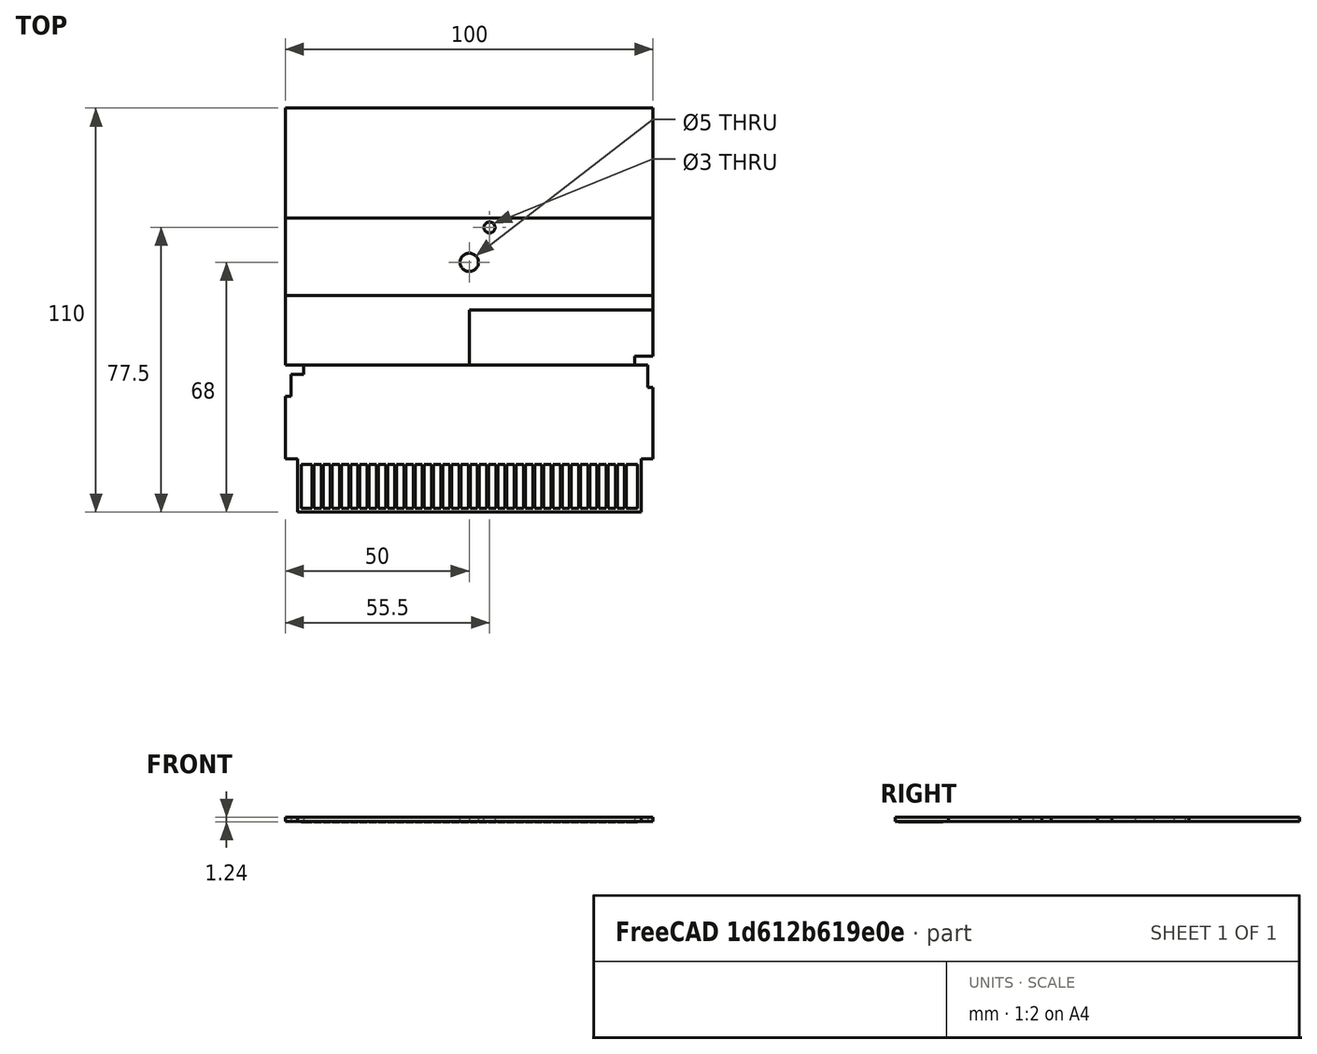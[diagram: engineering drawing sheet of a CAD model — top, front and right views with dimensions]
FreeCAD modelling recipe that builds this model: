
FCSTD DOCUMENT  (FreeCAD 0.20R29177 +426 (Git))
Label: NES-EWROM-01
License: Other
objects: TechDraw::DrawViewDimension×33, Sketcher::SketchObject×7, Part::Face×7, Part::Extrusion×5, App::Part×3, TechDraw::DrawProjGroupItem×3, Part::FeaturePython×2, TechDraw::DrawSVGTemplate×2, TechDraw::DrawPage×2, PartDesign::CoordinateSystem×1, TechDraw::DrawProjGroup×1, Spreadsheet::Sheet×1, TechDraw::DrawViewSpreadsheet×1
note: 22 computed .brp shape members not serialized (recipe doc carries the construction recipe); baked Part::Feature solids carry a one-line shape summary decoded from their .brp

FEATURE [PartDesign::CoordinateSystem] Local_CS_dc13
  AttacherType = Attacher::AttachEngine3D
  MapMode = 2
  Support = -> [X_Axis001]
FEATURE [App::Part] Step_Models_dc13
  Origin = -> Origin002
FEATURE [Part::FeaturePython] TopPads  # a2plus imported part (geometry in sourceFile) (typed FeaturePython)
  Placement = pos=(0,0,0.02) rot=(0,0,1;0rad)
  fixedPosition = true
FEATURE [Part::FeaturePython] BotPads  # a2plus imported part (geometry in sourceFile) (typed FeaturePython)
  Placement = pos=(0,0,0.38) rot=(0,0,1;0rad)
  fixedPosition = true
FEATURE [Sketcher::SketchObject] Sketch  label="TopSolderMask"
  FullyConstrained = true
  sketch-geometry (4):
    g0: LineSegment StartX=-46.75 StartY=-8 StartZ=0 EndX=46.75 EndY=-8 EndZ=0
    g1: LineSegment StartX=46.75 StartY=-8 StartZ=0 EndX=46.75 EndY=-14.5 EndZ=0
    g2: LineSegment StartX=46.75 StartY=-14.5 StartZ=0 EndX=-46.75 EndY=-14.5 EndZ=0
    g3: LineSegment StartX=-46.75 StartY=-14.5 StartZ=0 EndX=-46.75 EndY=-8 EndZ=0
  constraints (11):
    c: Coincident(g0,g1)
    c: Coincident(g1,g2)
    c: Coincident(g2,g3)
    c: Coincident(g3,g0)
    c: Horizontal(g2)
    c: Vertical(g1)
    c: Vertical(g3)
    c: DistanceY(g0,g-1) = 8
    c: DistanceY(g3,g3) = 6.5
    c: DistanceX(g2,g2) = 93.5
    c: Symmetric(g0,g0,g-2)
FEATURE [Part::Face] Face  label="TopSoldermask"
  FaceMakerClass = Part::FaceMakerBullseye
  Placement = pos=(0,0,0.02) rot=(0,0,1;0rad)
  Sources = -> [Sketch]
FEATURE [Sketcher::SketchObject] Sketch001  label="BotSoldermask"
  FullyConstrained = true
  Placement = pos=(0,0,-1.2) rot=(0,0,1;0rad)
  sketch-geometry (4):
    g0: LineSegment StartX=-46.75 StartY=-3.5 StartZ=0 EndX=46.75 EndY=-3.5 EndZ=0
    g1: LineSegment StartX=46.75 StartY=-3.5 StartZ=0 EndX=46.75 EndY=-14.5 EndZ=0
    g2: LineSegment StartX=46.75 StartY=-14.5 StartZ=0 EndX=-46.75 EndY=-14.5 EndZ=0
    g3: LineSegment StartX=-46.75 StartY=-14.5 StartZ=0 EndX=-46.75 EndY=-3.5 EndZ=0
  constraints (11):
    c: Coincident(g0,g1)
    c: Coincident(g1,g2)
    c: Coincident(g2,g3)
    c: Coincident(g3,g0)
    c: Horizontal(g0)
    c: Vertical(g1)
    c: Vertical(g3)
    c: Symmetric(g1,g2,g-2)
    c: DistanceY(g3,g3) = 11
    c: DistanceY(g0,g-1) = 3.5
    c: DistanceX(g2,g2) = 93.5
FEATURE [Part::Face] Face001  label="BotSolderMask"
  FaceMakerClass = Part::FaceMakerBullseye
  Placement = pos=(0,0,-0.02) rot=(0,0,1;0rad)
  Sources = -> [Sketch001]
FEATURE [TechDraw::DrawSVGTemplate] Template002  label="Template"
  EditableTexts = AUTHOR_NAME=Persune; DRAWING_TITLE=NES-EWROM-01; FC-DATE=2023-02-12; FC-REV=0.0.6; FC-SC=1:1; FC-SH=1/2; FC-SI=A4; FreeCAD_DRAWING=Unit in millimeters. Tolerance ±0.05mm.; SI-1=Outline made in Kicad. Drafting made in FreeCad.; SI-3=Base measurements assume 0.05 mm grid.
  Height = 210
  Orientation = 1
  Width = 297
FEATURE [Sketcher::SketchObject] Sketch002  label="CutTier1"
  FullyConstrained = true
  sketch-geometry (15):
    g0: LineSegment StartX=-50 StartY=0 StartZ=0 EndX=-46.75 EndY=0 EndZ=0
    g1: LineSegment StartX=-46.75 StartY=0 StartZ=0 EndX=-46.75 EndY=-14.5 EndZ=0
    g2: LineSegment StartX=46.75 StartY=-14.5 StartZ=0 EndX=46.75 EndY=0 EndZ=0
    g3: LineSegment StartX=46.75 StartY=0 StartZ=0 EndX=50 EndY=0 EndZ=0
    g4: LineSegment StartX=-50 StartY=17 StartZ=0 EndX=-50 EndY=0 EndZ=0
    g5: LineSegment StartX=-46.75 StartY=-14.5 StartZ=0 EndX=46.75 EndY=-14.5 EndZ=0
    g6: LineSegment StartX=-50 StartY=17 StartZ=0 EndX=-48.5 EndY=17 EndZ=0
    g7: LineSegment StartX=-48.5 StartY=17 StartZ=0 EndX=-48.5 EndY=23 EndZ=0
    g8: LineSegment StartX=-48.5 StartY=23 StartZ=0 EndX=-45 EndY=23 EndZ=0
    g9: LineSegment StartX=-45 StartY=23 StartZ=0 EndX=-45 EndY=25.5 EndZ=0
    g10: LineSegment StartX=50 StartY=0 StartZ=0 EndX=50 EndY=19.5 EndZ=0
    g11: LineSegment StartX=50 StartY=19.5 StartZ=0 EndX=48.5 EndY=19.5 EndZ=0
    g12: LineSegment StartX=45 StartY=25.5 StartZ=0 EndX=-45 EndY=25.5 EndZ=0
    g13: LineSegment StartX=45 StartY=25.5 StartZ=0 EndX=48.5 EndY=25.5 EndZ=0
    g14: LineSegment StartX=48.5 StartY=25.5 StartZ=0 EndX=48.5 EndY=19.5 EndZ=0
  constraints (45):
    c: PointOnObject(g0,g-1)
    c: PointOnObject(g0,g-1)
    c: Coincident(g1,g0)
    c: Vertical(g1)
    c: Vertical(g2)
    c: PointOnObject(g3,g-1)
    c: Horizontal(g3)
    c: Coincident(g4,g0)
    c: Vertical(g4)
    c: Symmetric(g0,g2,g-2)
    c: DistanceY(g1,g1) = 14.5
    c: Coincident(g5,g1)
    c: Coincident(g5,g2)
    c: Horizontal(g5)
    c: DistanceX(g5,g5) = 93.5
    c: DistanceX(g0,g0) = 3.25
    c: DistanceX(g0,g3) = 100
    c: DistanceY(g4,g4) = 17
    c: Coincident(g6,g4)
    c: Horizontal(g6)
    c: DistanceX(g6,g6) = 1.5
    c: Coincident(g7,g6)
    c: Vertical(g7)
    c: DistanceY(g7,g7) = 6
    c: Coincident(g8,g7)
    c: Horizontal(g8)
    c: DistanceX(g8,g8) = 3.5
    c: DistanceX(g3,g3) = 3.25
    c: Coincident(g8,g9)
    c: Vertical(g9)
    c: DistanceY(g9,g9) = 2.5
    c: Coincident(g10,g3)
    c: Vertical(g10)
    c: DistanceY(g10,g10) = 19.5
    c: Coincident(g10,g11)
    c: Horizontal(g11)
    c: Coincident(g12,g9)
    c: Horizontal(g12)
    c: DistanceX(g12,g12) = 90
    c: DistanceX(g11,g11) = 1.5
    c: Coincident(g12,g13)
    c: Horizontal(g13)
    c: Coincident(g13,g14)
    c: Coincident(g14,g11)
    c: Vertical(g14)
FEATURE [Sketcher::SketchObject] Sketch003  label="CutTier2"
  FullyConstrained = true
  sketch-geometry (6):
    g0: LineSegment StartX=-1.161e-13 StartY=25.5 StartZ=0 EndX=0 EndY=40.5 EndZ=0
    g1: LineSegment StartX=0 StartY=40.5 StartZ=0 EndX=50 EndY=40.5 EndZ=0
    g2: LineSegment StartX=50 StartY=40.5 StartZ=0 EndX=50 EndY=28 EndZ=0
    g3: LineSegment StartX=50 StartY=28 StartZ=0 EndX=45 EndY=28 EndZ=0
    g4: LineSegment StartX=45 StartY=28 StartZ=0 EndX=45 EndY=25.5 EndZ=0
    g5: LineSegment StartX=45 StartY=25.5 StartZ=0 EndX=-1.137e-13 EndY=25.5 EndZ=0
  constraints (18):
    c: PointOnObject(g0,g-2)
    c: PointOnObject(g0,g-2)
    c: Coincident(g0,g1)
    c: Horizontal(g1)
    c: Coincident(g1,g2)
    c: Coincident(g2,g3)
    c: Horizontal(g3)
    c: Coincident(g3,g4)
    c: Coincident(g4,g5)
    c: Coincident(g5,g0)
    c: Horizontal(g5)
    c: DistanceY(g-1,g0) = 25.5
    c: DistanceX(g5,g5) = 45
    c: Perpendicular(g5,g4)
    c: DistanceY(g4,g4) = 2.5
    c: DistanceX(g3,g3) = 5
    c: Perpendicular(g3,g2)
    c: DistanceY(g2,g2) = 12.5
FEATURE [Sketcher::SketchObject] Sketch004  label="CutTier3"
  FullyConstrained = true
  sketch-geometry (6):
    g0: LineSegment StartX=-50 StartY=25.5 StartZ=0 EndX=-50 EndY=44.5 EndZ=0
    g1: LineSegment StartX=-50 StartY=44.5 StartZ=0 EndX=50 EndY=44.5 EndZ=0
    g2: LineSegment StartX=50 StartY=44.5 StartZ=0 EndX=50 EndY=28 EndZ=0
    g3: LineSegment StartX=50 StartY=28 StartZ=0 EndX=45 EndY=28 EndZ=0
    g4: LineSegment StartX=45 StartY=28 StartZ=0 EndX=45 EndY=25.5 EndZ=0
    g5: LineSegment StartX=45 StartY=25.5 StartZ=0 EndX=-50 EndY=25.5 EndZ=0
  constraints (17):
    c: Vertical(g0)
    c: Coincident(g0,g1)
    c: Coincident(g1,g2)
    c: Vertical(g2)
    c: Coincident(g2,g3)
    c: Coincident(g3,g4)
    c: Coincident(g4,g5)
    c: Coincident(g5,g0)
    c: Horizontal(g5)
    c: DistanceY(g-1,g0) = 25.5
    c: Symmetric(g1,g0,g-2)
    c: DistanceY(g0,g0) = 19
    c: Perpendicular(g3,g2)
    c: Perpendicular(g4,g5)
    c: DistanceX(g5,g5) = 95
    c: DistanceY(g4,g4) = 2.5
    c: DistanceX(g3,g3) = 5
FEATURE [Sketcher::SketchObject] Sketch005  label="CutTier4"
  FullyConstrained = true
  sketch-geometry (6):
    g0: LineSegment StartX=-50 StartY=65.5 StartZ=0 EndX=50 EndY=65.5 EndZ=0
    g1: LineSegment StartX=-50 StartY=65.5 StartZ=0 EndX=-50 EndY=44.5 EndZ=0
    g2: LineSegment StartX=-50 StartY=44.5 StartZ=0 EndX=50 EndY=44.5 EndZ=0
    g3: LineSegment StartX=50 StartY=65.5 StartZ=0 EndX=50 EndY=44.5 EndZ=0
    g4: Circle CenterX=0 CenterY=53.5 CenterZ=0 NormalX=0 NormalY=0 NormalZ=1 AngleXU=0 Radius=2.5
    g5: Circle CenterX=5.5 CenterY=63 CenterZ=0 NormalX=0 NormalY=0 NormalZ=1 AngleXU=0 Radius=1.5
  constraints (17):
    c: DistanceY(g-1,g0) = 65.5
    c: Symmetric(g0,g0,g-2)
    c: DistanceX(g0,g0) = 100
    c: Coincident(g1,g0)
    c: Vertical(g1)
    c: Coincident(g2,g1)
    c: Horizontal(g2)
    c: Coincident(g3,g0)
    c: Coincident(g3,g2)
    c: Vertical(g3)
    c: DistanceY(g3,g3) = 21
    c: PointOnObject(g4,g-2)
    c: DistanceX(g-1,g5) = 5.5
    c: Radius(g5) = 1.5
    c: DistanceY(g-1,g5) = 63
    c: Radius(g4) = 2.5
    c: DistanceY(g-1,g4) = 53.5
FEATURE [Sketcher::SketchObject] Sketch006  label="CutTier5"
  FullyConstrained = true
  sketch-geometry (4):
    g0: LineSegment StartX=-50 StartY=65.5 StartZ=0 EndX=50 EndY=65.5 EndZ=0
    g1: LineSegment StartX=-50 StartY=65.5 StartZ=0 EndX=-50 EndY=95.5 EndZ=0
    g2: LineSegment StartX=-50 StartY=95.5 StartZ=0 EndX=50 EndY=95.5 EndZ=0
    g3: LineSegment StartX=50 StartY=95.5 StartZ=0 EndX=50 EndY=65.5 EndZ=0
  constraints (11):
    c: DistanceY(g-1,g0) = 65.5
    c: Symmetric(g0,g0,g-2)
    c: DistanceX(g0,g0) = 100
    c: Coincident(g0,g1)
    c: Vertical(g1)
    c: Coincident(g1,g2)
    c: Horizontal(g2)
    c: Coincident(g2,g3)
    c: Coincident(g3,g0)
    c: Vertical(g3)
    c: DistanceY(g1,g1) = 30
FEATURE [Part::Face] Face002  label="CutTier01"
  FaceMakerClass = Part::FaceMakerBullseye
  Sources = -> [Sketch002]
FEATURE [Part::Extrusion] Extrude  label="CutTier001"
  Base = -> Face002
  Dir = (0,0,1)
  DirMode = 2
  FaceMakerClass = Part::FaceMakerBullseye
  LengthFwd = -1.2
  LengthRev = 0
  Solid = false
  Symmetric = false
FEATURE [Part::Face] Face003  label="CutTier02"
  FaceMakerClass = Part::FaceMakerBullseye
  Sources = -> [Sketch003]
FEATURE [Part::Extrusion] Extrude001  label="CutTier002"
  Base = -> Face003
  Dir = (0,0,1)
  DirMode = 2
  FaceMakerClass = Part::FaceMakerBullseye
  LengthFwd = -1.2
  LengthRev = 0
  Solid = false
  Symmetric = false
FEATURE [Part::Face] Face004  label="CutTier03"
  FaceMakerClass = Part::FaceMakerBullseye
  Sources = -> [Sketch004]
FEATURE [Part::Extrusion] Extrude002  label="CutTier003"
  Base = -> Face004
  Dir = (0,0,1)
  DirMode = 2
  FaceMakerClass = Part::FaceMakerBullseye
  LengthFwd = -1.2
  LengthRev = 0
  Solid = false
  Symmetric = false
FEATURE [Part::Face] Face005  label="CutTier04"
  FaceMakerClass = Part::FaceMakerBullseye
  Sources = -> [Sketch005]
FEATURE [Part::Extrusion] Extrude003  label="CutTier004"
  Base = -> Face005
  Dir = (0,0,1)
  DirMode = 2
  FaceMakerClass = Part::FaceMakerBullseye
  LengthFwd = -1.2
  LengthRev = 0
  Solid = false
  Symmetric = false
FEATURE [Part::Face] Face006  label="CutTier05"
  FaceMakerClass = Part::FaceMakerBullseye
  Sources = -> [Sketch006]
FEATURE [Part::Extrusion] Extrude004  label="CutTier005"
  Base = -> Face006
  Dir = (0,0,1)
  DirMode = 2
  FaceMakerClass = Part::FaceMakerBullseye
  LengthFwd = -1.2
  LengthRev = 0
  Solid = false
  Symmetric = false
FEATURE [App::Part] Board_Geoms_dc13
  Group = -> [Sketch,BotPads,TopPads,Face,Sketch001,Face001,Face002,Sketch002,Extrude,Face003,Sketch003,Extrude001,Face004,Sketch004,Extrude002,Face005,Sketch005,Extrude003,Face006,Sketch006,Extrude004]
  Origin = -> Origin
FEATURE [App::Part] Board_dc13  label="NES-EWROM-01"
  Group = -> [Local_CS_dc13,Board_Geoms_dc13,Step_Models_dc13]
  Origin = -> Origin001
FEATURE [TechDraw::DrawProjGroupItem] ProjItem  label="Front"
  CoarseView = false
  Direction = (0,0,1)
  Focus = 100
  HardHidden = false
  IsoCount = 0
  IsoHidden = false
  IsoVisible = true
  LockPosition = true
  Perspective = false
  Rotation = 0
  RotationVector = (1,0,0)
  ScaleType = 2
  SeamHidden = false
  SeamVisible = true
  SmoothHidden = false
  SmoothVisible = true
  Source = -> [Board_dc13]
  Type = 0
  X = 0
  XDirection = (1,0,0)
  Y = 0
FEATURE [TechDraw::DrawProjGroupItem] ProjItem001  label="Rear"
  CoarseView = false
  Direction = (0,0,-1)
  Focus = 100
  HardHidden = false
  IsoCount = 0
  IsoHidden = false
  IsoVisible = true
  LockPosition = false
  Perspective = false
  Rotation = 0
  RotationVector = (1,0,0)
  ScaleType = 2
  SeamHidden = false
  SeamVisible = true
  SmoothHidden = false
  SmoothVisible = true
  Source = -> [Board_dc13]
  Type = 3
  X = 131.678
  XDirection = (-1,0,0)
  Y = 0
FEATURE [TechDraw::DrawProjGroupItem] ProjItem002  label="Left"
  CoarseView = false
  Direction = (-1,0,1e-16)
  Focus = 100
  HardHidden = false
  IsoCount = 0
  IsoHidden = false
  IsoVisible = true
  LockPosition = false
  Perspective = false
  Rotation = 0
  RotationVector = (1,0,0)
  ScaleType = 2
  SeamHidden = false
  SeamVisible = true
  SmoothHidden = false
  SmoothVisible = true
  Source = -> [Board_dc13]
  Type = 1
  X = 65.62
  XDirection = (1e-16,0,1)
  Y = 0
FEATURE [TechDraw::DrawProjGroup] ProjGroup
  Anchor = -> ProjItem
  AutoDistribute = false
  LockPosition = false
  ProjectionType = 0
  Rotation = 0
  ScaleType = 0
  Source = -> [Board_dc13]
  Views = -> [ProjItem,ProjItem001,ProjItem002]
  X = 88.8909
  Y = 129.504
  spacingX = 15
  spacingY = 15
FEATURE [Spreadsheet::Sheet] Spreadsheet  label="Board Dimensions"
  cells = A1=Designator; B1=Dimensions in Millimeters (± 0.5mm); C1=Description; A2=A; B2=100; C2=Board width; A3=A.1; B3=97; C3=Notched width; A4=A.2; B4=90; C4=Notched width; A5=A.3; B5=93.5; C5=Card edge width; A6=A.4; B6=50; C6=Tab width for cutout 2; A7=A.5; B7=50; C7=Hole center to PCB edge for cutout 4 / 5; A8=A.6; B8=44.5; C8=Hole center to PCB edge for cutout 4 / 5; A9=A.7; B9=3; C9=Hole diameter  for cutout 4 / 5; A10=A.8; B10=5; C10=Hole diameter  for cutout 4 / 5; A11=A.9; B11=3.5; C11=Notched width; A12=B.1; B12=25.5; C12=Board height for cutout 1; A13=B.2; B13=40.5; C13=Board height for cutout 2; A14=B.3; B14=44.5; C14=Board height for cutout 3; A15=B.4; B15=65.5; C15=Board height for cutout 4; A16=B.5; B16=95.5; C16=Board height for cutout 5; A17=B.6; B17=14.5; C17=Card edge depth; A18=B.7; B18=6; C18=Notch height; A19=B.8; B19=2.5; C19=Notch height; A20=B.9; B20=9; C20=Hole center to PCB edge for cutout 4 / 5; A21=B.10; B21=18.5; C21=Hole center to PCB edge for cutout 4 / 5; A22=C; B22=1.2; C22=Board thickness; A23=D.1; B23=6.5; C23=Card edge base to front soldermask keepout; A24=D.2; B24=3.5; C24=Card edge base to back soldermask keepout; A25=D.3; B25=1.5; C25=Card edge base to pad top; A26=D.4; B26=12; C26=Card edge pad height; A27=E.1; B27=1; C27=Card edge to edge pad side; A28=E.2; B28=3; C28=Edge pad width; A29=E.3; B29=0.5; C29=Distance between pads; A30=E.4; B30=2; C30=Pad width; A31=E.5; B31=2.5; C31=Pad spacing
FEATURE [TechDraw::DrawViewDimension] Dimension  label="A"
  AngleOverride = false
  Arbitrary = true
  ArbitraryTolerances = false
  EqualTolerance = true
  ExtensionAngle = 0
  FormatSpec = A
  FormatSpecOverTolerance = %+.2f
  FormatSpecUnderTolerance = %+.2f
  Inverted = false
  LineAngle = 0
  LockPosition = false
  MeasureType = 1
  OverTolerance = 0
  References2D = -> [ProjItem]
  Rotation = 0
  ScaleType = 0
  TheoreticalExact = false
  Type = 1
  UnderTolerance = 0
  X = 0
  Y = -72
FEATURE [TechDraw::DrawSVGTemplate] Template  label="Template001"
  EditableTexts = AUTHOR_NAME=Persune; DRAWING_TITLE=NES-EWROM-01; FC-DATE=2023-02-12; FC-REV=0.0.6; FC-SC=1:1; FC-SH=2/2; FC-SI=A4; FreeCAD_DRAWING=Unit in millimeters. Tolerance ±0.05mm.; SI-1=Outline made in Kicad. Drafting made in FreeCad.; SI-3=Base measurements assume 0.05 mm grid.
  Height = 210
  Orientation = 1
  Width = 297
FEATURE [TechDraw::DrawViewSpreadsheet] Sheet  label="Dimensions"
  CellEnd = C31
  CellStart = A1
  Font = Times New Roman
  LineWidth = 0.35
  LockPosition = false
  Rotation = 0
  Scale = 0.65
  ScaleType = 2
  Source = -> Spreadsheet
  Symbol = <blob: 21082 chars omitted>
  TextSize = 12
  X = 150.989
  Y = 122.446
FEATURE [TechDraw::DrawPage] Page  label="TechnicalDrawingPage2"
  KeepUpdated = true
  NextBalloonIndex = 1
  ProjectionType = 0
  Template = -> Template
  Views = -> [Sheet]
FEATURE [TechDraw::DrawViewDimension] Dimension001  label="A.1"
  AngleOverride = false
  Arbitrary = true
  ArbitraryTolerances = false
  EqualTolerance = true
  ExtensionAngle = 0
  FormatSpec = A.1
  FormatSpecOverTolerance = %+.2f
  FormatSpecUnderTolerance = %+.2f
  Inverted = false
  LineAngle = 0
  LockPosition = false
  MeasureType = 1
  OverTolerance = 0
  References2D = -> [ProjItem]
  Rotation = 0
  ScaleType = 0
  TheoreticalExact = false
  Type = 1
  UnderTolerance = 0
  X = 0
  Y = -69
FEATURE [TechDraw::DrawViewDimension] Dimension002  label="A.3"
  AngleOverride = false
  Arbitrary = true
  ArbitraryTolerances = false
  EqualTolerance = true
  ExtensionAngle = 0
  FormatSpec = A.3
  FormatSpecOverTolerance = %+.2f
  FormatSpecUnderTolerance = %+.2f
  Inverted = false
  LineAngle = 0
  LockPosition = false
  MeasureType = 1
  OverTolerance = 0
  References2D = -> [ProjItem]
  Rotation = 0
  ScaleType = 0
  TheoreticalExact = false
  Type = 1
  UnderTolerance = 0
  X = 0
  Y = -63
FEATURE [TechDraw::DrawViewDimension] Dimension003  label="A.4"
  AngleOverride = false
  Arbitrary = true
  ArbitraryTolerances = false
  EqualTolerance = true
  ExtensionAngle = 0
  FormatSpec = A.4
  FormatSpecOverTolerance = %+.2f
  FormatSpecUnderTolerance = %+.2f
  Inverted = false
  LineAngle = 0
  LockPosition = false
  MeasureType = 1
  OverTolerance = 0
  References2D = -> [ProjItem]
  Rotation = 0
  ScaleType = 0
  TheoreticalExact = false
  Type = 1
  UnderTolerance = 0
  X = 25
  Y = -3
FEATURE [TechDraw::DrawViewDimension] Dimension004  label="A.5"
  AngleOverride = false
  Arbitrary = true
  ArbitraryTolerances = false
  EqualTolerance = true
  ExtensionAngle = 0
  FormatSpec = A.5
  FormatSpecOverTolerance = %+.2f
  FormatSpecUnderTolerance = %+.2f
  Inverted = false
  LineAngle = 0
  LockPosition = false
  MeasureType = 1
  OverTolerance = 0
  References2D = -> [ProjItem]
  Rotation = 0
  ScaleType = 0
  TheoreticalExact = false
  Type = 1
  UnderTolerance = 0
  X = 25
  Y = 9
FEATURE [TechDraw::DrawViewDimension] Dimension005  label="A.6"
  AngleOverride = false
  Arbitrary = true
  ArbitraryTolerances = false
  EqualTolerance = true
  ExtensionAngle = 0
  FormatSpec = A.6
  FormatSpecOverTolerance = %+.2f
  FormatSpecUnderTolerance = %+.2f
  Inverted = false
  LineAngle = 0
  LockPosition = false
  MeasureType = 1
  OverTolerance = 0
  References2D = -> [ProjItem]
  Rotation = 0
  ScaleType = 0
  TheoreticalExact = false
  Type = 1
  UnderTolerance = 0
  X = 27.75
  Y = 16
FEATURE [TechDraw::DrawViewDimension] Dimension006  label="B.1"
  AngleOverride = false
  Arbitrary = true
  ArbitraryTolerances = false
  EqualTolerance = true
  ExtensionAngle = 0
  FormatSpec = B.1
  FormatSpecOverTolerance = %+.2f
  FormatSpecUnderTolerance = %+.2f
  Inverted = false
  LineAngle = 0
  LockPosition = false
  MeasureType = 1
  OverTolerance = 0
  References2D = -> [ProjItem]
  Rotation = 0
  ScaleType = 0
  TheoreticalExact = false
  Type = 2
  UnderTolerance = 0
  X = -53
  Y = -27.75
FEATURE [TechDraw::DrawViewDimension] Dimension007  label="B.2"
  AngleOverride = false
  Arbitrary = true
  ArbitraryTolerances = false
  EqualTolerance = true
  ExtensionAngle = 0
  FormatSpec = B.2
  FormatSpecOverTolerance = %+.2f
  FormatSpecUnderTolerance = %+.2f
  Inverted = false
  LineAngle = 0
  LockPosition = false
  MeasureType = 1
  OverTolerance = 0
  References2D = -> [ProjItem]
  Rotation = 0
  ScaleType = 0
  TheoreticalExact = false
  Type = 2
  UnderTolerance = 0
  X = -56
  Y = -20.25
FEATURE [TechDraw::DrawViewDimension] Dimension008  label="B.3"
  AngleOverride = false
  Arbitrary = true
  ArbitraryTolerances = false
  EqualTolerance = true
  ExtensionAngle = 0
  FormatSpec = B.3
  FormatSpecOverTolerance = %+.2f
  FormatSpecUnderTolerance = %+.2f
  Inverted = false
  LineAngle = 0
  LockPosition = false
  MeasureType = 1
  OverTolerance = 0
  References2D = -> [ProjItem]
  Rotation = 0
  ScaleType = 0
  TheoreticalExact = false
  Type = 2
  UnderTolerance = 0
  X = -60
  Y = -18.25
FEATURE [TechDraw::DrawViewDimension] Dimension009  label="B.4"
  AngleOverride = false
  Arbitrary = true
  ArbitraryTolerances = false
  EqualTolerance = true
  ExtensionAngle = 0
  FormatSpec = B.4
  FormatSpecOverTolerance = %+.2f
  FormatSpecUnderTolerance = %+.2f
  Inverted = false
  LineAngle = 0
  LockPosition = false
  MeasureType = 1
  OverTolerance = 0
  References2D = -> [ProjItem]
  Rotation = 0
  ScaleType = 0
  TheoreticalExact = false
  Type = 2
  UnderTolerance = 0
  X = -63
  Y = -7.75
FEATURE [TechDraw::DrawViewDimension] Dimension010  label="B.5"
  AngleOverride = false
  Arbitrary = true
  ArbitraryTolerances = false
  EqualTolerance = true
  ExtensionAngle = 0
  FormatSpec = B.5
  FormatSpecOverTolerance = %+.2f
  FormatSpecUnderTolerance = %+.2f
  Inverted = false
  LineAngle = 0
  LockPosition = false
  MeasureType = 1
  OverTolerance = 0
  References2D = -> [ProjItem]
  Rotation = 0
  ScaleType = 0
  TheoreticalExact = false
  Type = 2
  UnderTolerance = 0
  X = -66
  Y = 7.25
FEATURE [TechDraw::DrawViewDimension] Dimension011  label="B.6"
  AngleOverride = false
  Arbitrary = true
  ArbitraryTolerances = false
  EqualTolerance = true
  ExtensionAngle = 0
  FormatSpec = B.6
  FormatSpecOverTolerance = %+.2f
  FormatSpecUnderTolerance = %+.2f
  Inverted = false
  LineAngle = 0
  LockPosition = false
  MeasureType = 1
  OverTolerance = 0
  References2D = -> [ProjItem]
  Rotation = 0
  ScaleType = 0
  TheoreticalExact = false
  Type = 2
  UnderTolerance = 0
  X = -66
  Y = -47.75
FEATURE [TechDraw::DrawViewDimension] Dimension014  label="D.4"
  AngleOverride = false
  Arbitrary = true
  ArbitraryTolerances = false
  EqualTolerance = true
  ExtensionAngle = 0
  FormatSpec = D.4
  FormatSpecOverTolerance = %+.2f
  FormatSpecUnderTolerance = %+.2f
  Inverted = false
  LineAngle = 0
  LockPosition = false
  MeasureType = 1
  OverTolerance = 0
  References2D = -> [ProjItem]
  Rotation = 0
  ScaleType = 0
  TheoreticalExact = false
  Type = 2
  UnderTolerance = 0
  X = -57
  Y = -66
FEATURE [TechDraw::DrawViewDimension] Dimension016  label="D.1"
  AngleOverride = false
  Arbitrary = true
  ArbitraryTolerances = false
  EqualTolerance = true
  ExtensionAngle = 0
  FormatSpec = D.1
  FormatSpecOverTolerance = %+.2f
  FormatSpecUnderTolerance = %+.2f
  Inverted = false
  LineAngle = 0
  LockPosition = false
  MeasureType = 1
  OverTolerance = 0
  References2D = -> [ProjItem]
  Rotation = 0
  ScaleType = 0
  TheoreticalExact = false
  Type = 2
  UnderTolerance = 0
  X = -63
  Y = -60
FEATURE [TechDraw::DrawViewDimension] Dimension017  label="D.2"
  AngleOverride = false
  Arbitrary = true
  ArbitraryTolerances = false
  EqualTolerance = true
  ExtensionAngle = 0
  FormatSpec = D.2
  FormatSpecOverTolerance = %+.2f
  FormatSpecUnderTolerance = %+.2f
  Inverted = false
  LineAngle = 0
  LockPosition = false
  MeasureType = 1
  OverTolerance = 0
  References2D = -> [ProjItem001]
  Rotation = 0
  ScaleType = 0
  TheoreticalExact = false
  Type = 2
  UnderTolerance = 0
  X = -53
  Y = -51
FEATURE [TechDraw::DrawViewDimension] Dimension018  label="C"
  AngleOverride = false
  Arbitrary = true
  ArbitraryTolerances = false
  EqualTolerance = true
  ExtensionAngle = 0
  FormatSpec = C
  FormatSpecOverTolerance = %+.2f
  FormatSpecUnderTolerance = %+.2f
  Inverted = false
  LineAngle = 0
  LockPosition = false
  MeasureType = 1
  OverTolerance = 0
  References2D = -> [ProjItem002]
  Rotation = 0
  ScaleType = 0
  TheoreticalExact = false
  Type = 1
  UnderTolerance = 0
  X = -9
  Y = -63
FEATURE [TechDraw::DrawViewDimension] Dimension019  label="D.3"
  AngleOverride = false
  Arbitrary = true
  ArbitraryTolerances = false
  EqualTolerance = true
  ExtensionAngle = 0
  FormatSpec = D.3
  FormatSpecOverTolerance = %+.2f
  FormatSpecUnderTolerance = %+.2f
  Inverted = false
  LineAngle = 0
  LockPosition = false
  MeasureType = 1
  OverTolerance = 0
  References2D = -> [ProjItem]
  Rotation = 0
  ScaleType = 0
  TheoreticalExact = false
  Type = 2
  UnderTolerance = 0
  X = -60
  Y = -63
FEATURE [TechDraw::DrawViewDimension] Dimension020  label="E.1"
  AngleOverride = false
  Arbitrary = true
  ArbitraryTolerances = false
  EqualTolerance = true
  ExtensionAngle = 0
  FormatSpec = E.1
  FormatSpecOverTolerance = %+.2f
  FormatSpecUnderTolerance = %+.2f
  Inverted = false
  LineAngle = 0
  LockPosition = false
  MeasureType = 1
  OverTolerance = 0
  References2D = -> [ProjItem001]
  Rotation = 0
  ScaleType = 0
  TheoreticalExact = false
  Type = 1
  UnderTolerance = 0
  X = -30
  Y = -63
FEATURE [TechDraw::DrawViewDimension] Dimension021  label="E.2"
  AngleOverride = false
  Arbitrary = true
  ArbitraryTolerances = false
  EqualTolerance = true
  ExtensionAngle = 0
  FormatSpec = E.2
  FormatSpecOverTolerance = %+.2f
  FormatSpecUnderTolerance = %+.2f
  Inverted = false
  LineAngle = 0
  LockPosition = false
  MeasureType = 1
  OverTolerance = 0
  References2D = -> [ProjItem001]
  Rotation = 0
  ScaleType = 0
  TheoreticalExact = false
  Type = 1
  UnderTolerance = 0
  X = -30
  Y = -66
FEATURE [TechDraw::DrawViewDimension] Dimension022  label="E.3"
  AngleOverride = false
  Arbitrary = true
  ArbitraryTolerances = false
  EqualTolerance = true
  ExtensionAngle = 0
  FormatSpec = E.3
  FormatSpecOverTolerance = %+.2f
  FormatSpecUnderTolerance = %+.2f
  Inverted = false
  LineAngle = 0
  LockPosition = false
  MeasureType = 1
  OverTolerance = 0
  References2D = -> [ProjItem001]
  Rotation = 0
  ScaleType = 0
  TheoreticalExact = false
  Type = 1
  UnderTolerance = 0
  X = -30
  Y = -69
FEATURE [TechDraw::DrawViewDimension] Dimension023  label="E.4"
  AngleOverride = false
  Arbitrary = true
  ArbitraryTolerances = false
  EqualTolerance = true
  ExtensionAngle = 0
  FormatSpec = E.4
  FormatSpecOverTolerance = %+.2f
  FormatSpecUnderTolerance = %+.2f
  Inverted = false
  LineAngle = 0
  LockPosition = false
  MeasureType = 1
  OverTolerance = 0
  References2D = -> [ProjItem001]
  Rotation = 0
  ScaleType = 0
  TheoreticalExact = false
  Type = 1
  UnderTolerance = 0
  X = -30
  Y = -72
FEATURE [TechDraw::DrawViewDimension] Dimension024  label="E.5"
  AngleOverride = false
  Arbitrary = true
  ArbitraryTolerances = false
  EqualTolerance = true
  ExtensionAngle = 0
  FormatSpec = E.5
  FormatSpecOverTolerance = %+.2f
  FormatSpecUnderTolerance = %+.2f
  Inverted = false
  LineAngle = 0
  LockPosition = false
  MeasureType = 1
  OverTolerance = 0
  References2D = -> [ProjItem001]
  Rotation = 0
  ScaleType = 0
  TheoreticalExact = false
  Type = 1
  UnderTolerance = 0
  X = -30
  Y = -75
FEATURE [TechDraw::DrawViewDimension] Dimension025  label="B.7"
  AngleOverride = false
  Arbitrary = true
  ArbitraryTolerances = false
  EqualTolerance = true
  ExtensionAngle = 0
  FormatSpec = B.7
  FormatSpecOverTolerance = %+.2f
  FormatSpecUnderTolerance = %+.2f
  Inverted = false
  LineAngle = 0
  LockPosition = false
  MeasureType = 1
  OverTolerance = 0
  References2D = -> [ProjItem]
  Rotation = 0
  ScaleType = 0
  TheoreticalExact = false
  Type = 2
  UnderTolerance = 0
  X = -42
  Y = -30
FEATURE [TechDraw::DrawViewDimension] Dimension026  label="B.8"
  AngleOverride = false
  Arbitrary = true
  ArbitraryTolerances = false
  EqualTolerance = true
  ExtensionAngle = 0
  FormatSpec = B.8
  FormatSpecOverTolerance = %+.2f
  FormatSpecUnderTolerance = %+.2f
  Inverted = false
  LineAngle = 0
  LockPosition = false
  MeasureType = 1
  OverTolerance = 0
  References2D = -> [ProjItem]
  Rotation = 0
  ScaleType = 0
  TheoreticalExact = false
  Type = 2
  UnderTolerance = 0
  X = -36
  Y = -30
FEATURE [TechDraw::DrawViewDimension] Dimension027  label="B.07"
  AngleOverride = false
  Arbitrary = true
  ArbitraryTolerances = false
  EqualTolerance = true
  ExtensionAngle = 0
  FormatSpec = B.7
  FormatSpecOverTolerance = %+.2f
  FormatSpecUnderTolerance = %+.2f
  Inverted = false
  LineAngle = 0
  LockPosition = false
  MeasureType = 1
  OverTolerance = 0
  References2D = -> [ProjItem]
  Rotation = 0
  ScaleType = 0
  TheoreticalExact = false
  Type = 2
  UnderTolerance = 0
  X = 42
  Y = -30
FEATURE [TechDraw::DrawViewDimension] Dimension028  label="B.08"
  AngleOverride = false
  Arbitrary = true
  ArbitraryTolerances = false
  EqualTolerance = true
  ExtensionAngle = 0
  FormatSpec = B.8
  FormatSpecOverTolerance = %+.2f
  FormatSpecUnderTolerance = %+.2f
  Inverted = false
  LineAngle = 0
  LockPosition = false
  MeasureType = 1
  OverTolerance = 0
  References2D = -> [ProjItem]
  Rotation = 0
  ScaleType = 0
  TheoreticalExact = false
  Type = 2
  UnderTolerance = 0
  X = 36
  Y = -30
FEATURE [TechDraw::DrawViewDimension] Dimension029  label="A.2"
  AngleOverride = false
  Arbitrary = true
  ArbitraryTolerances = false
  EqualTolerance = true
  ExtensionAngle = 0
  FormatSpec = A.2
  FormatSpecOverTolerance = %+.2f
  FormatSpecUnderTolerance = %+.2f
  Inverted = false
  LineAngle = 0
  LockPosition = false
  MeasureType = 1
  OverTolerance = 0
  References2D = -> [ProjItem]
  Rotation = 0
  ScaleType = 0
  TheoreticalExact = false
  Type = 1
  UnderTolerance = 0
  X = 0
  Y = -66
FEATURE [TechDraw::DrawViewDimension] Dimension030  label="A.9"
  AngleOverride = false
  Arbitrary = true
  ArbitraryTolerances = false
  EqualTolerance = true
  ExtensionAngle = 0
  FormatSpec = A.9
  FormatSpecOverTolerance = %+.2f
  FormatSpecUnderTolerance = %+.2f
  Inverted = false
  LineAngle = 0
  LockPosition = false
  MeasureType = 1
  OverTolerance = 0
  References2D = -> [ProjItem]
  Rotation = 0
  ScaleType = 0
  TheoreticalExact = false
  Type = 1
  UnderTolerance = 0
  X = -30
  Y = -6
FEATURE [TechDraw::DrawViewDimension] Dimension031  label="A.09"
  AngleOverride = false
  Arbitrary = true
  ArbitraryTolerances = false
  EqualTolerance = true
  ExtensionAngle = 0
  FormatSpec = A.9
  FormatSpecOverTolerance = %+.2f
  FormatSpecUnderTolerance = %+.2f
  Inverted = false
  LineAngle = 0
  LockPosition = false
  MeasureType = 1
  OverTolerance = 0
  References2D = -> [ProjItem]
  Rotation = 0
  ScaleType = 0
  TheoreticalExact = false
  Type = 1
  UnderTolerance = 0
  X = 34
  Y = -6
FEATURE [TechDraw::DrawViewDimension] Dimension032  label="A.7"
  AngleOverride = false
  Arbitrary = true
  ArbitraryTolerances = false
  EqualTolerance = true
  ExtensionAngle = 0
  FormatSpec = A.7
  FormatSpecOverTolerance = %+.2f
  FormatSpecUnderTolerance = %+.2f
  Inverted = false
  LineAngle = 0
  LockPosition = false
  MeasureType = 1
  OverTolerance = 0
  References2D = -> [ProjItem]
  Rotation = 0
  ScaleType = 0
  TheoreticalExact = false
  Type = 5
  UnderTolerance = 0
  X = -15
  Y = 21
FEATURE [TechDraw::DrawViewDimension] Dimension033  label="A.8"
  AngleOverride = false
  Arbitrary = true
  ArbitraryTolerances = false
  EqualTolerance = true
  ExtensionAngle = 0
  FormatSpec = A.8
  FormatSpecOverTolerance = %+.2f
  FormatSpecUnderTolerance = %+.2f
  Inverted = false
  LineAngle = 0
  LockPosition = false
  MeasureType = 1
  OverTolerance = 0
  References2D = -> [ProjItem]
  Rotation = 0
  ScaleType = 0
  TheoreticalExact = false
  Type = 5
  UnderTolerance = 0
  X = -15
  Y = 18
FEATURE [TechDraw::DrawViewDimension] Dimension034  label="B.9"
  AngleOverride = false
  Arbitrary = true
  ArbitraryTolerances = false
  EqualTolerance = true
  ExtensionAngle = 0
  FormatSpec = B.9
  FormatSpecOverTolerance = %+.2f
  FormatSpecUnderTolerance = %+.2f
  Inverted = false
  LineAngle = 0
  LockPosition = false
  MeasureType = 1
  OverTolerance = 0
  References2D = -> [ProjItem]
  Rotation = 0
  ScaleType = 0
  TheoreticalExact = false
  Type = 2
  UnderTolerance = 0
  X = -21
  Y = 33
FEATURE [TechDraw::DrawViewDimension] Dimension035  label="B.10"
  AngleOverride = false
  Arbitrary = true
  ArbitraryTolerances = false
  EqualTolerance = true
  ExtensionAngle = 0
  FormatSpec = B.10
  FormatSpecOverTolerance = %+.2f
  FormatSpecUnderTolerance = %+.2f
  Inverted = false
  LineAngle = 0
  LockPosition = false
  MeasureType = 1
  OverTolerance = 0
  References2D = -> [ProjItem]
  Rotation = 0
  ScaleType = 0
  TheoreticalExact = false
  Type = 2
  UnderTolerance = 0
  X = -28
  Y = 33
FEATURE [TechDraw::DrawPage] Page002  label="TechnicalDrawingPage1"
  KeepUpdated = true
  NextBalloonIndex = 1
  ProjectionType = 0
  Template = -> Template002
  Views = -> [ProjGroup,Dimension,Dimension001,Dimension002,Dimension003,Dimension004,Dimension005,Dimension006,Dimension007,Dimension008,Dimension009,Dimension010,Dimension011,Dimension014,Dimension016,Dimension017,Dimension018,Dimension019,Dimension020,Dimension021,Dimension022,Dimension023,Dimension024,Dimension025,Dimension026,Dimension027,Dimension028,Dimension029,Dimension030,Dimension031,Dimension032,+3 more]
